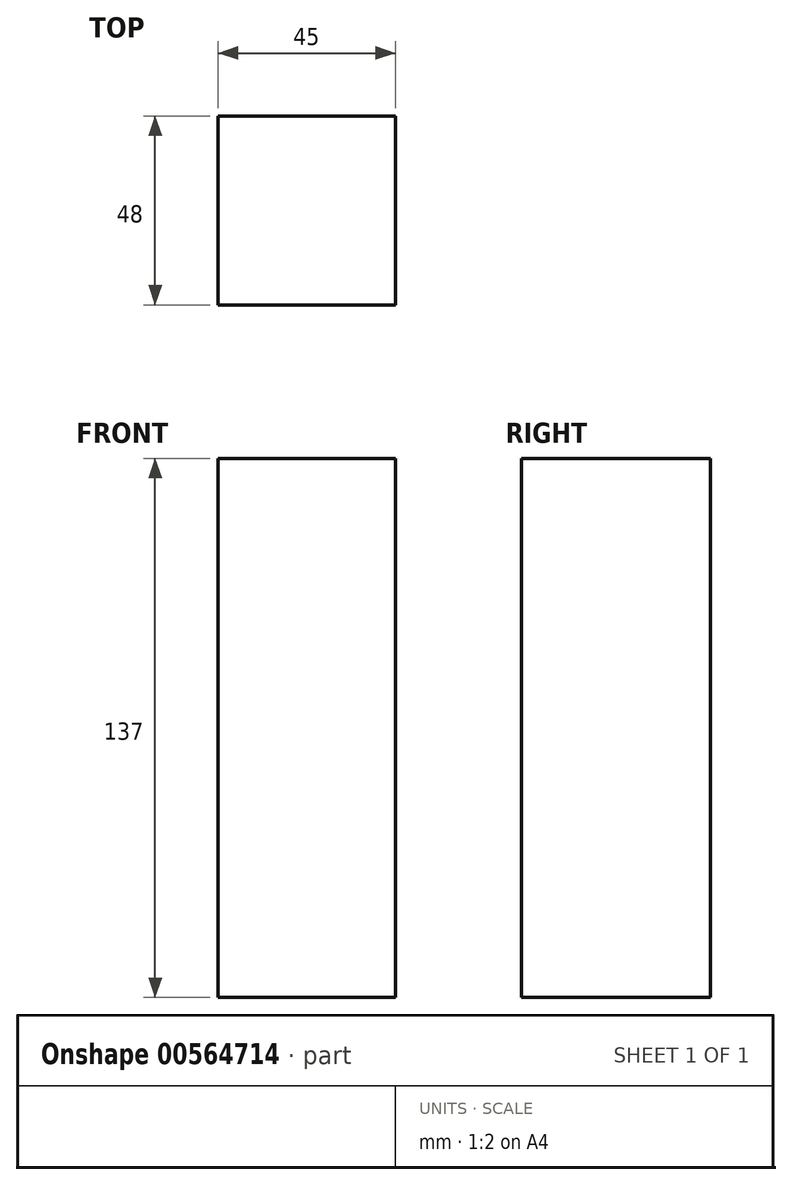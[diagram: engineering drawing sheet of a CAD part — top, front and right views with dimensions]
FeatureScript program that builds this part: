
annotation { "Feature Type Name" : "Feature", "Feature Type Description" : "" }
export const myFeature = defineFeature(function(context is Context, id is Id, definition is map)
    precondition{}
    {
        {
            var Q0;
            Q0=qCreatedBy(makeId("Front.planeOp"),FACE);
            var sketch = newSketch(context, id + "F0", { "sketchPlane" : qUnion([Q0])});
            skLineSegment(sketch, "E0.bottom", {"start": v(-100.18, 64.5) * mm, "end": v(-55.18, 64.5) * mm});
            skLineSegment(sketch, "E0.top", {"start": v(-100.18, -72.5) * mm, "end": v(-55.18, -72.5) * mm});
            skLineSegment(sketch, "E0.left", {"start": v(-100.18, 64.5) * mm, "end": v(-100.18, -72.5) * mm});
            skLineSegment(sketch, "E0.right", {"start": v(-55.18, 64.5) * mm, "end": v(-55.18, -72.5) * mm});
            skSolve(sketch);
        }
        {
            var Q0;
            Q0 = qSketchRegion(id + "F0", true);
            extrude(context, id + "F1", {"entities" : qUnion([Q0]), "depth" : 48 * mm, "offsetDistance" : 25 * mm});
        }
    });
